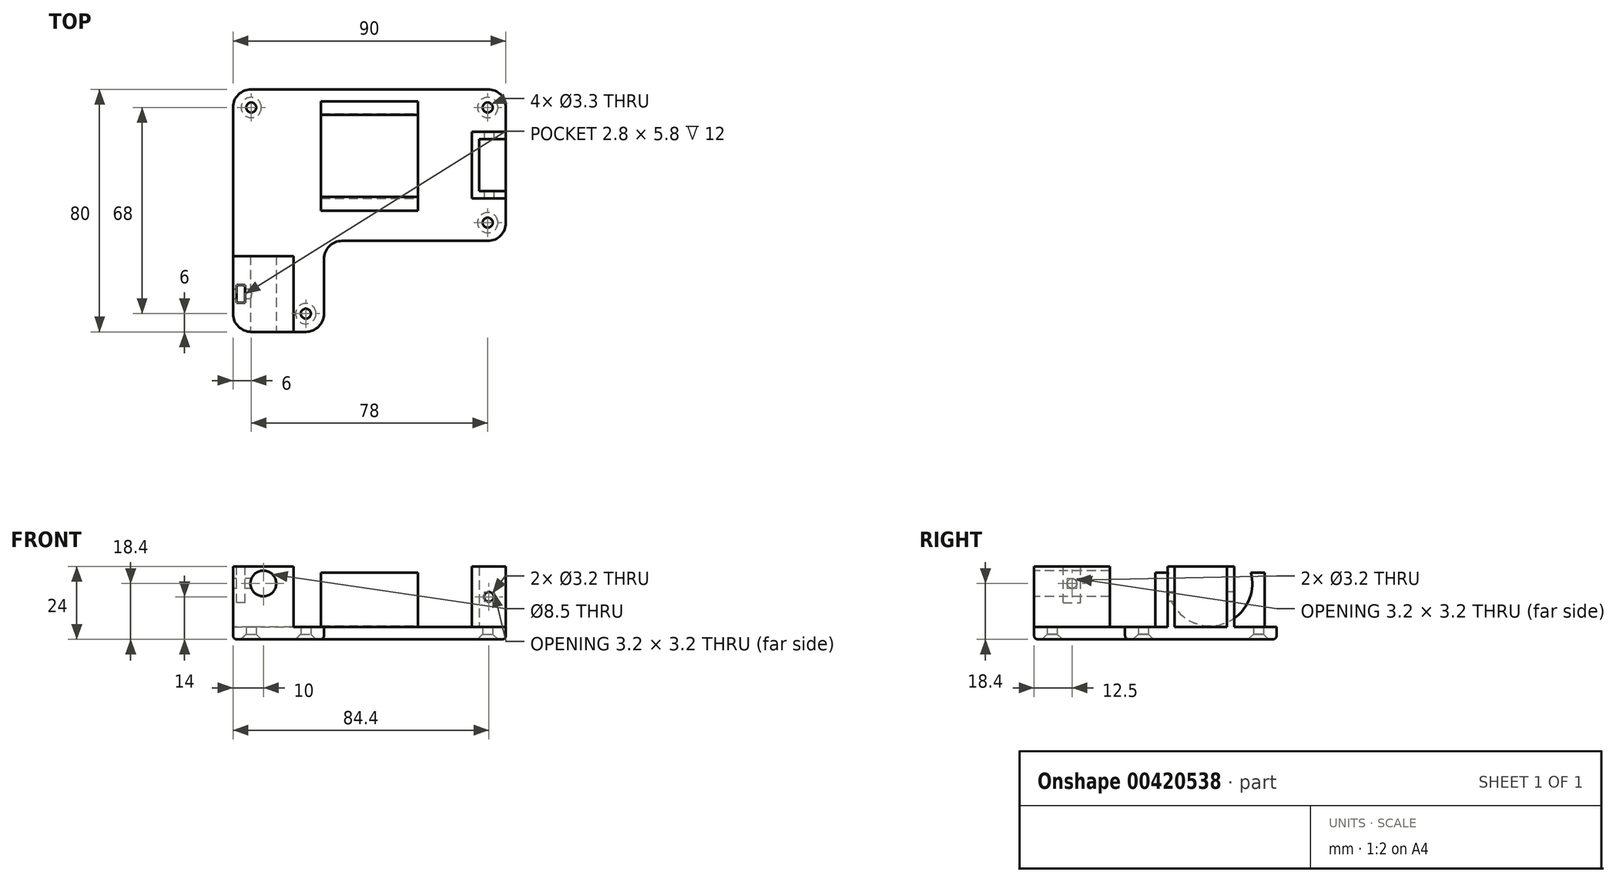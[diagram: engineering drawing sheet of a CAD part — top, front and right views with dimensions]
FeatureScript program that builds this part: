
annotation { "Feature Type Name" : "Feature", "Feature Type Description" : "" }
export const myFeature = defineFeature(function(context is Context, id is Id, definition is map)
    precondition{}
    {
        {
            var Q0;
            Q0=qCreatedBy(makeId("Top.planeOp"),FACE);
            var sketch = newSketch(context, id + "F0", { "sketchPlane" : qUnion([Q0])});
            skLineSegment(sketch, "E0.bottom", {"start": v(-15, -40) * mm, "end": v(-45, -40) * mm});
            skLineSegment(sketch, "E0.top", {"start": v(45, 40) * mm, "end": v(-45, 40) * mm});
            skLineSegment(sketch, "E0.left", {"start": v(45, -10) * mm, "end": v(45, 40) * mm});
            skLineSegment(sketch, "E0.right", {"start": v(-45, -40) * mm, "end": v(-45, 40) * mm});
            skPoint(sketch, "E0.middle", {"position": v(0, 0) * mm});
            skLineSegment(sketch, "E1.top", {"start": v(45, -10) * mm, "end": v(-15, -10) * mm});
            skLineSegment(sketch, "E1.right", {"start": v(-15, -40) * mm, "end": v(-15, -10) * mm});
            skPoint(sketch, "E2.orphan", {"position": v(45, -40) * mm});
            skSolve(sketch);
        }
        {
            var Q0;
            Q0=makeQuery(id+"F0.imprint","IMPRINT",FACE,{"disambiguationData":[TD([[makeQuery(id+"F0.imprint","IMPRINT",EDGE,{"derivedFrom":sQuery(id+"F0.wireOp",EDGE,"E0.bottom")}),-1.0]])]});
            extrude(context, id + "F1", {"entities" : qUnion([Q0]), "depth" : 4 * mm});
        }
        {
            var Q0;
            Q0=makeQuery(id+"F1.opExtrude","CAP_FACE",FACE,{"disambiguationData":[OSD([sQuery(id+"F0.wireOp",EDGE,"E0.bottom"),sQuery(id+"F0.wireOp",EDGE,"E0.top"),sQuery(id+"F0.wireOp",EDGE,"E0.left"),sQuery(id+"F0.wireOp",EDGE,"E0.right")])],"isStart":false});
            var sketch = newSketch(context, id + "F2", { "sketchPlane" : qUnion([Q0])});
            skLineSegment(sketch, "E3.bottom", {"start": v(-45, -40) * mm, "end": v(-25, -40) * mm});
            skLineSegment(sketch, "E3.top", {"start": v(-45, -15) * mm, "end": v(-25, -15) * mm});
            skLineSegment(sketch, "E3.left", {"start": v(-45, -40) * mm, "end": v(-45, -15) * mm});
            skLineSegment(sketch, "E3.right", {"start": v(-25, -40) * mm, "end": v(-25, -15) * mm});
            skLineSegment(sketch, "E4.bottom", {"start": v(16, 0) * mm, "end": v(-16, 0) * mm});
            skLineSegment(sketch, "E4.top", {"start": v(16, 36) * mm, "end": v(-16, 36) * mm});
            skLineSegment(sketch, "E4.left", {"start": v(16, 0) * mm, "end": v(16, 36) * mm});
            skLineSegment(sketch, "E4.right", {"start": v(-16, 0) * mm, "end": v(-16, 36) * mm});
            skPoint(sketch, "E4.middle", {"position": v(0, 18) * mm});
            skLineSegment(sketch, "E5.bottom", {"start": v(36.2, 4) * mm, "end": v(33.8, 4) * mm});
            skLineSegment(sketch, "E5.top", {"start": v(36.2, 26) * mm, "end": v(33.8, 26) * mm});
            skLineSegment(sketch, "E5.left", {"start": v(36.2, 4) * mm, "end": v(36.2, 26) * mm});
            skLineSegment(sketch, "E5.right", {"start": v(33.8, 4) * mm, "end": v(33.8, 26) * mm});
            skPoint(sketch, "E5.middle", {"position": v(35, 15) * mm});
            skPoint(sketch, "E5.middle.positionSnap0", {"position": v(45, 15) * mm});
            skPoint(sketch, "E5.centerSnap0", {"position": v(45, 15) * mm});
            skLineSegment(sketch, "E6.bottom", {"start": v(36.2, 26) * mm, "end": v(45, 26) * mm});
            skLineSegment(sketch, "E6.top", {"start": v(36.2, 23.6) * mm, "end": v(45, 23.6) * mm});
            skLineSegment(sketch, "E6.left", {"start": v(36.2, 26) * mm, "end": v(36.2, 23.6) * mm});
            skLineSegment(sketch, "E6.right", {"start": v(45, 26) * mm, "end": v(45, 23.6) * mm});
            skLineSegment(sketch, "E7.bottom", {"start": v(36.2, 4) * mm, "end": v(45, 4) * mm});
            skLineSegment(sketch, "E7.top", {"start": v(36.2, 6.4) * mm, "end": v(45, 6.4) * mm});
            skLineSegment(sketch, "E7.left", {"start": v(36.2, 4) * mm, "end": v(36.2, 6.4) * mm});
            skLineSegment(sketch, "E7.right", {"start": v(45, 4) * mm, "end": v(45, 6.4) * mm});
            skSolve(sketch);
        }
        {
            var Q0;
            Q0=makeQuery(id+"F2.imprint","IMPRINT",FACE,{"disambiguationData":[TD([[makeQuery(id+"F2.imprint","IMPRINT",EDGE,{"derivedFrom":sQuery(id+"F2.wireOp",EDGE,"E4.bottom")}),-1.0]])]});
            extrude(context, id + "F3", {"entities" : qUnion([Q0]), "operationType" : NewBodyOperationType.ADD, "depth" : 18 * mm});
        }
        {
            var Q0;
            Q0=makeQuery(id+"F3.opExtrude","SWEPT_FACE",FACE,{"disambiguationData":[OSD([sQuery(id+"F2.wireOp",EDGE,"E4.left")])]});
            var sketch = newSketch(context, id + "F4", { "sketchPlane" : qUnion([Q0])});
            skCircle(sketch, "E8", {"center": v(18, 18.4) * mm, "radius": 14 * mm});
            skPoint(sketch, "E8.centerSnap0", {"position": v(18, 4) * mm});
            skSolve(sketch);
        }
        {
            var Q0;
            {var subQ0=sQuery(id+"F4.wireOp",EDGE,"E8");var subQ1=makeQuery(id+"F3.opExtrude","CAP_EDGE",EDGE,{"disambiguationData":[OSD([sQuery(id+"F2.wireOp",EDGE,"E4.left")])],"isStart":false});var subQ2=makeQuery(id+"F4.imprint","INTERSECT",VERTEX,{"disambiguationData":[OD(0.0)],"derivedFrom":[subQ1,subQ0]});Q0=makeQuery(id+"F4.imprint","IMPRINT",FACE,{"disambiguationData":[TD([[makeQuery(id+"F4.imprint","IMPRINT",EDGE,{"disambiguationData":[TD([[subQ2,-1.0]])],"derivedFrom":subQ0}),1.0]])]});}
            extrude(context, id + "F5", {"entities" : qUnion([Q0]), "operationType" : NewBodyOperationType.REMOVE, "endBound" : BoundingType.UP_TO_NEXT, "oppositeDirection" : true, "depth" : 25 * mm});
        }
        {
            var Q0;
            Q0=makeQuery(id+"F2.imprint","IMPRINT",FACE,{"disambiguationData":[TD([[makeQuery(id+"F2.imprint","IMPRINT",EDGE,{"derivedFrom":sQuery(id+"F2.wireOp",EDGE,"E3.bottom")}),-1.0]])]});
            extrude(context, id + "F6", {"entities" : qUnion([Q0]), "operationType" : NewBodyOperationType.ADD, "depth" : 20 * mm});
        }
        {
            var Q0;
            Q0=makeQuery(id+"F6.boolean.opBoolean","MERGE",FACE,{"derivedFrom":[makeQuery(id+"F1.opExtrude","SWEPT_FACE",FACE,{"disambiguationData":[OSD([sQuery(id+"F0.wireOp",EDGE,"E0.bottom")])]}),makeQuery(id+"F6.opExtrude","SWEPT_FACE",FACE,{"disambiguationData":[OSD([sQuery(id+"F2.wireOp",EDGE,"E3.bottom")])]})]});
            var sketch = newSketch(context, id + "F7", { "sketchPlane" : qUnion([Q0])});
            skCircle(sketch, "E9", {"center": v(-35, 18.4) * mm, "radius": 4.25 * mm});
            skPoint(sketch, "E9.centerSnap0", {"position": v(-35, 24) * mm});
            skSolve(sketch);
        }
        {
            var Q0;
            Q0=makeQuery(id+"F7.imprint","IMPRINT",FACE,{"disambiguationData":[TD([[makeQuery(id+"F7.imprint","IMPRINT",EDGE,{"derivedFrom":sQuery(id+"F7.wireOp",EDGE,"E9")}),1.0]])]});
            extrude(context, id + "F8", {"entities" : qUnion([Q0]), "operationType" : NewBodyOperationType.REMOVE, "endBound" : BoundingType.UP_TO_NEXT, "oppositeDirection" : true, "depth" : 25 * mm});
        }
        {
            var Q0;
            Q0=makeQuery(id+"F6.opExtrude","CAP_FACE",FACE,{"disambiguationData":[OSD([sQuery(id+"F2.wireOp",EDGE,"E3.bottom"),sQuery(id+"F2.wireOp",EDGE,"E3.top"),sQuery(id+"F2.wireOp",EDGE,"E3.left"),sQuery(id+"F2.wireOp",EDGE,"E3.right")])],"isStart":false});
            var sketch = newSketch(context, id + "F9", { "sketchPlane" : qUnion([Q0])});
            skLineSegment(sketch, "E10.bottom", {"start": v(-41, -30.4) * mm, "end": v(-43.8, -30.4) * mm});
            skLineSegment(sketch, "E10.top", {"start": v(-41, -24.6) * mm, "end": v(-43.8, -24.6) * mm});
            skLineSegment(sketch, "E10.left", {"start": v(-41, -30.4) * mm, "end": v(-41, -24.6) * mm});
            skLineSegment(sketch, "E10.right", {"start": v(-43.8, -30.4) * mm, "end": v(-43.8, -24.6) * mm});
            skPoint(sketch, "E10.middle", {"position": v(-42.4, -27.5) * mm});
            skPoint(sketch, "E10.middle.positionSnap0", {"position": v(-45, -27.5) * mm});
            skPoint(sketch, "E10.centerSnap0", {"position": v(-45, -27.5) * mm});
            skSolve(sketch);
        }
        {
            var Q0;
            Q0=makeQuery(id+"F9.imprint","IMPRINT",FACE,{"disambiguationData":[TD([[makeQuery(id+"F9.imprint","IMPRINT",EDGE,{"derivedFrom":sQuery(id+"F9.wireOp",EDGE,"E10.bottom")}),-1.0]])]});
            extrude(context, id + "F10", {"entities" : qUnion([Q0]), "operationType" : NewBodyOperationType.REMOVE, "oppositeDirection" : true, "depth" : 12 * mm});
        }
        {
            var Q0;
            Q0=makeQuery(id+"F6.boolean.opBoolean","MERGE",FACE,{"derivedFrom":[makeQuery(id+"F1.opExtrude","SWEPT_FACE",FACE,{"disambiguationData":[OSD([sQuery(id+"F0.wireOp",EDGE,"E0.right")])]}),makeQuery(id+"F6.opExtrude","SWEPT_FACE",FACE,{"disambiguationData":[OSD([sQuery(id+"F2.wireOp",EDGE,"E3.left")])]})]});
            var sketch = newSketch(context, id + "F11", { "sketchPlane" : qUnion([Q0])});
            skCircle(sketch, "E11", {"center": v(27.5, 18.4) * mm, "radius": 1.6 * mm});
            skPoint(sketch, "E11.centerSnap0", {"position": v(27.5, 24) * mm});
            skSolve(sketch);
        }
        {
            var Q0;
            Q0=makeQuery(id+"F11.imprint","IMPRINT",FACE,{"disambiguationData":[TD([[makeQuery(id+"F11.imprint","IMPRINT",EDGE,{"derivedFrom":sQuery(id+"F11.wireOp",EDGE,"E11")}),1.0]])]});
            extrude(context, id + "F12", {"entities" : qUnion([Q0]), "operationType" : NewBodyOperationType.REMOVE, "oppositeDirection" : true, "depth" : 10 * mm});
        }
        {
            var Q0;
            Q0=makeQuery(id+"F1.opExtrude","SWEPT_EDGE",EDGE,{"disambiguationData":[OSD([sQuery(id+"F0.wireOp",EDGE,"E0.bottom"),sQuery(id+"F0.wireOp",EDGE,"E1.right")])]});
            var Q1;
            Q1=makeQuery(id+"F1.opExtrude","SWEPT_EDGE",EDGE,{"disambiguationData":[OSD([sQuery(id+"F0.wireOp",EDGE,"E0.left"),sQuery(id+"F0.wireOp",EDGE,"E1.top")])]});
            var Q2;
            Q2=makeQuery(id+"F1.opExtrude","SWEPT_EDGE",EDGE,{"disambiguationData":[OSD([sQuery(id+"F0.wireOp",EDGE,"E0.top"),sQuery(id+"F0.wireOp",EDGE,"E0.left")])]});
            var Q3;
            Q3=makeQuery(id+"F1.opExtrude","SWEPT_EDGE",EDGE,{"disambiguationData":[OSD([sQuery(id+"F0.wireOp",EDGE,"E0.top"),sQuery(id+"F0.wireOp",EDGE,"E0.right")])]});
            var Q4;
            Q4=makeQuery(id+"F6.boolean.opBoolean","MERGE",EDGE,{"derivedFrom":[makeQuery(id+"F1.opExtrude","SWEPT_EDGE",EDGE,{"disambiguationData":[OSD([sQuery(id+"F0.wireOp",EDGE,"E0.bottom"),sQuery(id+"F0.wireOp",EDGE,"E0.right")])]}),makeQuery(id+"F6.opExtrude","SWEPT_EDGE",EDGE,{"disambiguationData":[OSD([sQuery(id+"F2.wireOp",EDGE,"E3.bottom"),sQuery(id+"F2.wireOp",EDGE,"E3.left")])]})]});
            var Q5;
            Q5=makeQuery(id+"F1.opExtrude","SWEPT_EDGE",EDGE,{"disambiguationData":[OSD([sQuery(id+"F0.wireOp",EDGE,"E1.top"),sQuery(id+"F0.wireOp",EDGE,"E1.right")])]});
            fillet(context, id + "F13", {"entities" : qUnion([Q0, Q1, Q2, Q3, Q4, Q5]), "radius" : 6 * mm, "tangentPropagation" : true, "allowEdgeOverflow" : false});
        }
        {
            var Q0;
            Q0=makeQuery(id+"F2.imprint","IMPRINT",FACE,{"disambiguationData":[TD([[makeQuery(id+"F2.imprint","IMPRINT",EDGE,{"derivedFrom":sQuery(id+"F2.wireOp",EDGE,"E5.bottom")}),-1.0]])]});
            var Q1;
            Q1=makeQuery(id+"F2.imprint","IMPRINT",FACE,{"disambiguationData":[TD([[makeQuery(id+"F2.imprint","IMPRINT",EDGE,{"derivedFrom":sQuery(id+"F2.wireOp",EDGE,"E7.bottom")}),1.0]])]});
            var Q2;
            Q2=makeQuery(id+"F2.imprint","IMPRINT",FACE,{"disambiguationData":[TD([[makeQuery(id+"F2.imprint","IMPRINT",EDGE,{"derivedFrom":sQuery(id+"F2.wireOp",EDGE,"E6.bottom")}),-1.0]])]});
            extrude(context, id + "F14", {"entities" : qUnion([Q0, Q1, Q2]), "operationType" : NewBodyOperationType.ADD, "depth" : 20 * mm});
        }
        {
            var Q0;
            Q0=makeQuery(id+"F14.opExtrude","SWEPT_FACE",FACE,{"disambiguationData":[OSD([sQuery(id+"F2.wireOp",EDGE,"E5.bottom"),sQuery(id+"F2.wireOp",EDGE,"E7.bottom")])]});
            var sketch = newSketch(context, id + "F15", { "sketchPlane" : qUnion([Q0])});
            skCircle(sketch, "E12", {"center": v(39.4, 14) * mm, "radius": 1.6 * mm});
            skPoint(sketch, "E12.centerSnap0", {"position": v(39.4, 24) * mm});
            skSolve(sketch);
        }
        {
            var Q0;
            Q0=makeQuery(id+"F15.imprint","IMPRINT",FACE,{"disambiguationData":[TD([[makeQuery(id+"F15.imprint","IMPRINT",EDGE,{"derivedFrom":sQuery(id+"F15.wireOp",EDGE,"E12")}),1.0]])]});
            var Q1;
            Q1=makeQuery(id+"F14.opExtrude","SWEPT_FACE",FACE,{"disambiguationData":[OSD([sQuery(id+"F2.wireOp",EDGE,"E5.top"),sQuery(id+"F2.wireOp",EDGE,"E6.bottom")])]});
            extrude(context, id + "F16", {"entities" : qUnion([Q0]), "operationType" : NewBodyOperationType.REMOVE, "endBound" : BoundingType.UP_TO_SURFACE, "oppositeDirection" : true, "endBoundEntityFace" : qUnion([Q1]), "depth" : 25 * mm});
        }
        {
            var Q0;
            Q0=makeQuery(id+"F1.opExtrude","CAP_FACE",FACE,{"disambiguationData":[OSD([sQuery(id+"F0.wireOp",EDGE,"E0.bottom"),sQuery(id+"F0.wireOp",EDGE,"E0.top"),sQuery(id+"F0.wireOp",EDGE,"E0.left"),sQuery(id+"F0.wireOp",EDGE,"E0.right"),sQuery(id+"F0.wireOp",EDGE,"E1.top"),sQuery(id+"F0.wireOp",EDGE,"E1.right")])],"isStart":true});
            var sketch = newSketch(context, id + "F17", { "sketchPlane" : qUnion([Q0])});
            skPoint(sketch, "E13", {"position": v(39, -34) * mm});
            skPoint(sketch, "E14", {"position": v(39, 4) * mm});
            skPoint(sketch, "E15", {"position": v(-39, -34) * mm});
            skPoint(sketch, "E16", {"position": v(-39, 34) * mm});
            skPoint(sketch, "E17", {"position": v(-21, 34) * mm});
            skSolve(sketch);
        }
        {
            var Q0;
            Q0=sQuery(id+"F17.wireOp",VERTEX,"E17");
            var Q1;
            Q1=sQuery(id+"F17.wireOp",VERTEX,"E14");
            var Q2;
            Q2=sQuery(id+"F17.wireOp",VERTEX,"E13");
            var Q3;
            Q3=sQuery(id+"F17.wireOp",VERTEX,"E15");
            var Q4;
            Q4=makeQuery(id+"F1.opExtrude","SWEPT_BODY",BODY,{"disambiguationData":[OSD([sQuery(id+"F0.wireOp",EDGE,"E0.bottom"),sQuery(id+"F0.wireOp",EDGE,"E0.top"),sQuery(id+"F0.wireOp",EDGE,"E0.left"),sQuery(id+"F0.wireOp",EDGE,"E0.right"),sQuery(id+"F0.wireOp",EDGE,"E1.top"),sQuery(id+"F0.wireOp",EDGE,"E1.right")])]});
            hole(context, id + "F18", {"style" : HoleStyle.C_SINK, "endStyle" : HoleEndStyle.THROUGH, "standardTappedOrClearance" : lookupTablePath({ "standard" : "ISO", "fit" : "Normal", "size" : "M3", "type" : "Clearance" }), "standardBlindInLast" : lookupTablePath({ "fit" : "Standard", "standard" : "ISO", "size" : "M3", "type" : "Clearance" }), "holeDiameter" : 3.3 * mm, "cSinkDiameter" : 6.72 * mm, "cSinkAngle" : 90 * degree, "isTappedThrough" : true, "tappedDepth" : 12 * mm, "tapClearance" : 3, "locations" : qUnion([Q0, Q1, Q2, Q3]), "scope" : qUnion([Q4])});
        }
        {
            var Q0;
            Q0=makeQuery(id+"F1.opExtrude","CAP_EDGE",EDGE,{"disambiguationData":[OSD([sQuery(id+"F0.wireOp",EDGE,"E0.top")])],"isStart":true});
            var Q1;
            {var subQ0=sQuery(id+"F0.wireOp",EDGE,"E0.right");var subQ1=sQuery(id+"F0.wireOp",EDGE,"E0.top");Q1=makeQuery(id+"F13.opFillet","BLEND_EDGE",EDGE,{"blendedFrom":[makeQuery(id+"F1.opExtrude","SWEPT_EDGE",EDGE,{"disambiguationData":[OSD([subQ1,subQ0])]}),makeQuery(id+"F1.opExtrude","CAP_FACE",FACE,{"disambiguationData":[OSD([sQuery(id+"F0.wireOp",EDGE,"E0.bottom"),subQ1,sQuery(id+"F0.wireOp",EDGE,"E0.left"),subQ0,sQuery(id+"F0.wireOp",EDGE,"E1.top"),sQuery(id+"F0.wireOp",EDGE,"E1.right")])],"isStart":true})],"blendedInto":[makeQuery(id+"F1.opExtrude","CAP_FACE",FACE,{"disambiguationData":[OSD([sQuery(id+"F0.wireOp",EDGE,"E0.bottom"),subQ1,sQuery(id+"F0.wireOp",EDGE,"E0.left"),subQ0,sQuery(id+"F0.wireOp",EDGE,"E1.top"),sQuery(id+"F0.wireOp",EDGE,"E1.right")])],"isStart":true})]});}
            fillet(context, id + "F19", {"entities" : qUnion([Q0, Q1]), "radius" : 1.2 * mm, "tangentPropagation" : true, "allowEdgeOverflow" : false});
        }
    });
